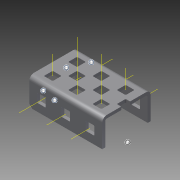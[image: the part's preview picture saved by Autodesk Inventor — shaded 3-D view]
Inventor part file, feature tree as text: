
AUTODESK INVENTOR PART (.ipt)
format: ipt  version: 2015 (Build 190159000, 159)  size: 1,917,952 bytes
history: native  units: in
note: dims shown in document units (in); Inventor stores cm internally (conversion verified against a paired STEP export)
features: other x21, pattern_linear x3, sheet_metal_op x1, extrude x1, imported_body x1, sketch x1
ambient origin geometry x8: Origin, YZ Plane, XZ Plane, XY Plane, X Axis, Y Axis, Z Axis, Center Point
bodies: Body1 (feature_tree)
feature tree (28):
  sheet_metal_op  "Fold1"
  other  "C-Channel"
  extrude  "length cut"  Depth=0.5in
  other  "top axis"
  other  "inner axis"
  other  "front axis"
  other  "back axis"
  pattern_linear  "top axes"  Spacing1=0.5in  [1 undecoded]
  pattern_linear  "inner axes"  Spacing1=0.5in  [1 undecoded]
  pattern_linear  "horiz axes"  Spacing1=-1.5in  [1 undecoded]
  other  "right plane"
  imported_body  "Base1"
  sketch  "Sketch1"  dims[d1=0.0in d4=0.5in d5=0.7874in d7=0.5in d10=0.5in d13=0.5in d14=-1.5in d15=0.0in d16=0.0in d17=0.0in d18=0.0in d19=0.0in]
  other  "Work Point1"
  other  "Work Point2"
  other  "Work Point3"
  other  "Work Point4"
  other  "Work Axis5"
  other  "Work Axis6"
  other  "Work Axis11"
  other  "Work Axis12"
  other  "Work Axis13"
  other  "Work Axis18"
  other  "Work Axis23"
  other  "Work Axis24"
  other  "Work Axis30"
  other  "Work Axis31"
  other  "left plane"
note: 3 required parameter values undecoded (feature->parameter linkage not recoverable at this tier; creation-order binding heuristic only, values carry confidence <= 0.55)
